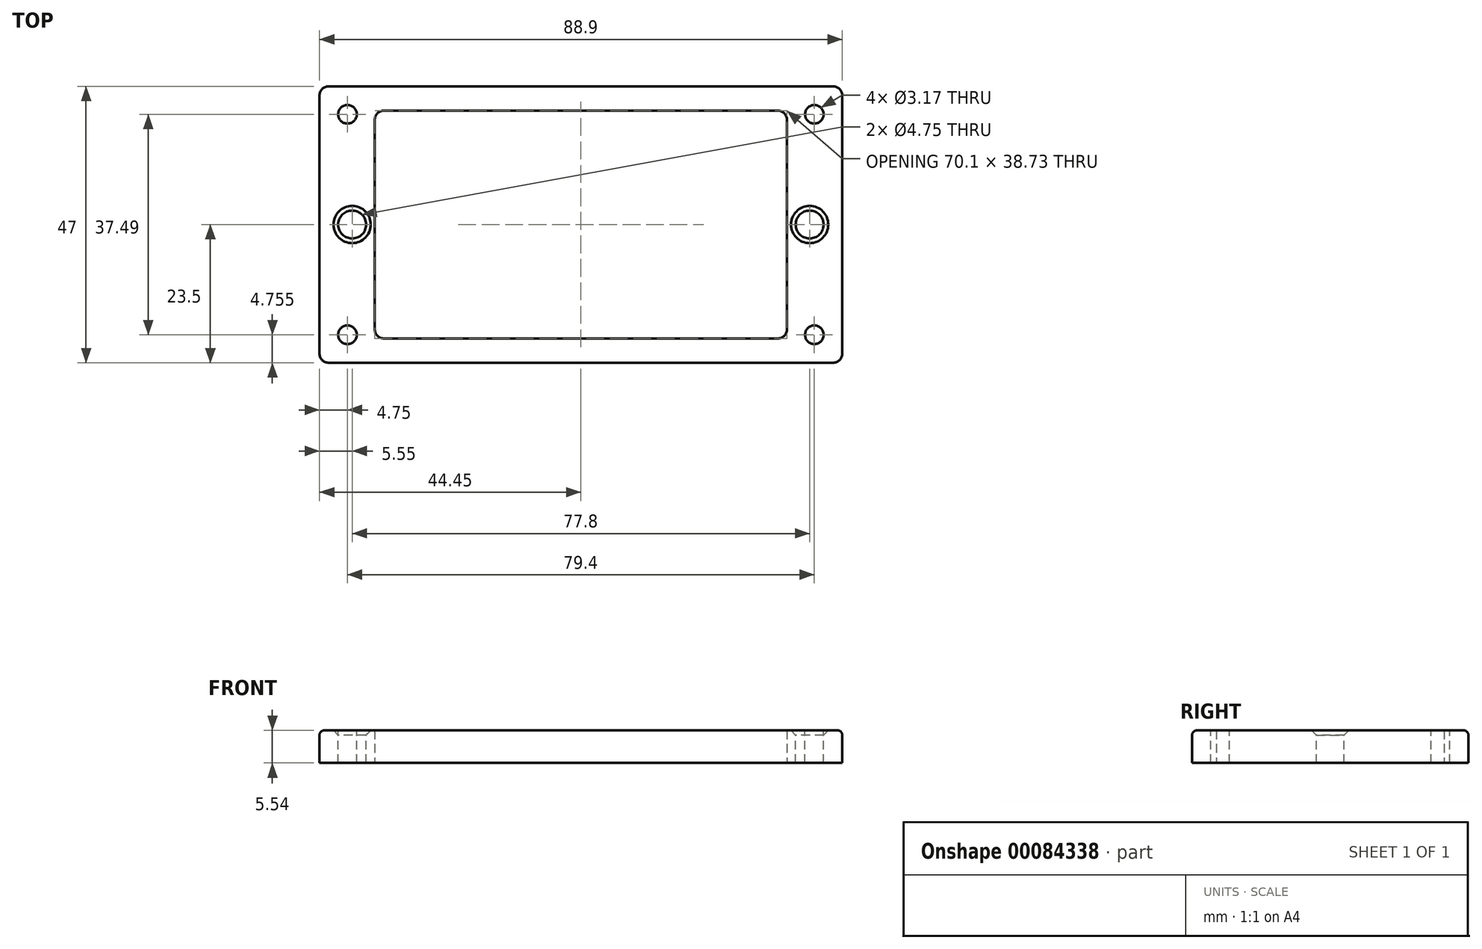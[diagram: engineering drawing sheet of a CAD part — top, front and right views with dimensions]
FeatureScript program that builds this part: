
annotation { "Feature Type Name" : "Feature", "Feature Type Description" : "" }
export const myFeature = defineFeature(function(context is Context, id is Id, definition is map)
    precondition{}
    {
        {
            var Q0;
            Q0=qCreatedBy(makeId("Top.planeOp"),FACE);
            var sketch = newSketch(context, id + "F0", { "sketchPlane" : qUnion([Q0]), "disableImprinting" : false});
            skLineSegment(sketch, "E0.bottom", {"start": v(44.45, 23.5) * mm, "end": v(-44.45, 23.5) * mm});
            skLineSegment(sketch, "E0.top", {"start": v(44.45, -23.5) * mm, "end": v(-44.45, -23.5) * mm});
            skLineSegment(sketch, "E0.left", {"start": v(44.45, 23.5) * mm, "end": v(44.45, -23.5) * mm});
            skLineSegment(sketch, "E0.right", {"start": v(-44.45, 23.5) * mm, "end": v(-44.45, -23.5) * mm});
            skPoint(sketch, "E0.middle", {"position": v(0, 0) * mm});
            skLineSegment(sketch, "E1.bottom", {"start": v(35.05, 19.37) * mm, "end": v(-35.05, 19.37) * mm});
            skLineSegment(sketch, "E1.top", {"start": v(35.05, -19.37) * mm, "end": v(-35.05, -19.37) * mm});
            skLineSegment(sketch, "E1.left", {"start": v(35.05, 19.37) * mm, "end": v(35.05, -19.37) * mm});
            skLineSegment(sketch, "E1.right", {"start": v(-35.05, 19.37) * mm, "end": v(-35.05, -19.37) * mm});
            skSolve(sketch);
        }
        {
            var Q0;
            Q0=makeQuery(id+"F0.imprint","IMPRINT",FACE,{"disambiguationData":[TD([[makeQuery(id+"F0.imprint","IMPRINT",EDGE,{"derivedFrom":sQuery(id+"F0.wireOp",EDGE,"E0.bottom")}),1.0]])]});
            var sketch = newSketch(context, id + "F1", { "sketchPlane" : qUnion([Q0]), "disableImprinting" : false});
            skLineSegment(sketch, "E2", {"start": v(-44.45, 0) * mm, "end": v(-35.05, 0) * mm, "construction": true});
            skLineSegment(sketch, "E3.0", {"start": v(-44.45, 23.5) * mm, "end": v(-44.45, -23.5) * mm});
            skLineSegment(sketch, "E4.0", {"start": v(-35.05, 19.37) * mm, "end": v(-35.05, -19.37) * mm});
            skPoint(sketch, "E5", {"position": v(-38.9, 0) * mm});
            skCircle(sketch, "E6", {"center": v(-38.9, 0) * mm, "radius": 2.37 * mm});
            skCircle(sketch, "E7.MirrorC", {"center": v(38.9, 0) * mm, "radius": 2.37 * mm});
            skSolve(sketch);
        }
        {
            var Q0;
            Q0=makeQuery(id+"F0.imprint","IMPRINT",FACE,{"disambiguationData":[TD([[makeQuery(id+"F0.imprint","IMPRINT",EDGE,{"derivedFrom":sQuery(id+"F0.wireOp",EDGE,"E0.bottom")}),1.0]])]});
            extrude(context, id + "F2", {"entities" : qUnion([Q0]), "depth" : 5.54 * mm, "symmetric" : true});
        }
        {
            var Q0;
            Q0 = qSketchRegion(id + "F1", true);
            extrude(context, id + "F3", {"entities" : qUnion([Q0]), "operationType" : NewBodyOperationType.REMOVE, "oppositeDirection" : true, "depth" : 25.4 * mm, "symmetric" : true});
        }
        {
            var Q0;
            Q0=makeQuery(id+"F2.opExtrude","CAP_FACE",FACE,{"disambiguationData":[OSD([sQuery(id+"F0.wireOp",EDGE,"E0.bottom"),sQuery(id+"F0.wireOp",EDGE,"E0.top"),sQuery(id+"F0.wireOp",EDGE,"E0.left"),sQuery(id+"F0.wireOp",EDGE,"E0.right"),sQuery(id+"F0.wireOp",EDGE,"E1.bottom"),sQuery(id+"F0.wireOp",EDGE,"E1.top"),sQuery(id+"F0.wireOp",EDGE,"E1.left"),sQuery(id+"F0.wireOp",EDGE,"E1.right")])],"isStart":false});
            var sketch = newSketch(context, id + "F4", { "sketchPlane" : qUnion([Q0])});
            skCircle(sketch, "E8", {"center": v(-39.7, 18.75) * mm, "radius": 1.59 * mm});
            skCircle(sketch, "E9.MirrorC", {"center": v(-39.7, -18.75) * mm, "radius": 1.59 * mm});
            skCircle(sketch, "E10.MirrorC", {"center": v(39.7, 18.75) * mm, "radius": 1.59 * mm});
            skCircle(sketch, "E11.MirrorC", {"center": v(39.7, -18.75) * mm, "radius": 1.59 * mm});
            skSolve(sketch);
        }
        {
            var Q0;
            Q0 = qSketchRegion(id + "F4", true);
            extrude(context, id + "F5", {"entities" : qUnion([Q0]), "operationType" : NewBodyOperationType.REMOVE, "oppositeDirection" : true, "depth" : 25.4 * mm});
        }
        {
            var Q0;
            Q0=makeQuery(id+"F2.opExtrude","SWEPT_EDGE",EDGE,{"disambiguationData":[OSD([sQuery(id+"F0.wireOp",EDGE,"E0.bottom"),sQuery(id+"F0.wireOp",EDGE,"E0.right")])]});
            var Q1;
            Q1=makeQuery(id+"F2.opExtrude","SWEPT_EDGE",EDGE,{"disambiguationData":[OSD([sQuery(id+"F0.wireOp",EDGE,"E0.top"),sQuery(id+"F0.wireOp",EDGE,"E0.right")])]});
            var Q2;
            Q2=makeQuery(id+"F2.opExtrude","SWEPT_EDGE",EDGE,{"disambiguationData":[OSD([sQuery(id+"F0.wireOp",EDGE,"E0.bottom"),sQuery(id+"F0.wireOp",EDGE,"E0.left")])]});
            var Q3;
            Q3=makeQuery(id+"F2.opExtrude","SWEPT_EDGE",EDGE,{"disambiguationData":[OSD([sQuery(id+"F0.wireOp",EDGE,"E0.top"),sQuery(id+"F0.wireOp",EDGE,"E0.left")])]});
            var Q4;
            Q4=makeQuery(id+"F2.opExtrude","SWEPT_EDGE",EDGE,{"disambiguationData":[OSD([sQuery(id+"F0.wireOp",EDGE,"E1.bottom"),sQuery(id+"F0.wireOp",EDGE,"E1.left")])]});
            var Q5;
            Q5=makeQuery(id+"F2.opExtrude","SWEPT_EDGE",EDGE,{"disambiguationData":[OSD([sQuery(id+"F0.wireOp",EDGE,"E1.top"),sQuery(id+"F0.wireOp",EDGE,"E1.left")])]});
            var Q6;
            Q6=makeQuery(id+"F2.opExtrude","SWEPT_EDGE",EDGE,{"disambiguationData":[OSD([sQuery(id+"F0.wireOp",EDGE,"E1.bottom"),sQuery(id+"F0.wireOp",EDGE,"E1.right")])]});
            var Q7;
            Q7=makeQuery(id+"F2.opExtrude","SWEPT_EDGE",EDGE,{"disambiguationData":[OSD([sQuery(id+"F0.wireOp",EDGE,"E1.top"),sQuery(id+"F0.wireOp",EDGE,"E1.right")])]});
            fillet(context, id + "F6", {"entities" : qUnion([Q0, Q1, Q2, Q3, Q4, Q5, Q6, Q7]), "radius" : 1.57 * mm, "tangentPropagation" : true, "allowEdgeOverflow" : false});
        }
        {
            var Q0;
            Q0=makeQuery(id+"F2.opExtrude","CAP_EDGE",EDGE,{"disambiguationData":[OSD([sQuery(id+"F0.wireOp",EDGE,"E0.bottom")])],"isStart":false});
            var Q1;
            {var subQ0=sQuery(id+"F0.wireOp",EDGE,"E0.right");var subQ1=sQuery(id+"F0.wireOp",EDGE,"E0.bottom");Q1=makeQuery(id+"F6.opFillet","BLEND_EDGE",EDGE,{"blendedFrom":[makeQuery(id+"F2.opExtrude","SWEPT_EDGE",EDGE,{"disambiguationData":[OSD([subQ1,subQ0])]}),makeQuery(id+"F2.opExtrude","CAP_FACE",FACE,{"disambiguationData":[OSD([subQ1,sQuery(id+"F0.wireOp",EDGE,"E0.top"),sQuery(id+"F0.wireOp",EDGE,"E0.left"),subQ0,sQuery(id+"F0.wireOp",EDGE,"E1.bottom"),sQuery(id+"F0.wireOp",EDGE,"E1.top"),sQuery(id+"F0.wireOp",EDGE,"E1.left"),sQuery(id+"F0.wireOp",EDGE,"E1.right")])],"isStart":false})],"blendedInto":[makeQuery(id+"F2.opExtrude","CAP_FACE",FACE,{"disambiguationData":[OSD([subQ1,sQuery(id+"F0.wireOp",EDGE,"E0.top"),sQuery(id+"F0.wireOp",EDGE,"E0.left"),subQ0,sQuery(id+"F0.wireOp",EDGE,"E1.bottom"),sQuery(id+"F0.wireOp",EDGE,"E1.top"),sQuery(id+"F0.wireOp",EDGE,"E1.left"),sQuery(id+"F0.wireOp",EDGE,"E1.right")])],"isStart":false})]});}
            var Q2;
            Q2=makeQuery(id+"F2.opExtrude","CAP_EDGE",EDGE,{"disambiguationData":[OSD([sQuery(id+"F0.wireOp",EDGE,"E0.right")])],"isStart":false});
            var Q3;
            {var subQ0=sQuery(id+"F0.wireOp",EDGE,"E0.right");var subQ1=sQuery(id+"F0.wireOp",EDGE,"E0.top");Q3=makeQuery(id+"F6.opFillet","BLEND_EDGE",EDGE,{"blendedFrom":[makeQuery(id+"F2.opExtrude","SWEPT_EDGE",EDGE,{"disambiguationData":[OSD([subQ1,subQ0])]}),makeQuery(id+"F2.opExtrude","CAP_FACE",FACE,{"disambiguationData":[OSD([sQuery(id+"F0.wireOp",EDGE,"E0.bottom"),subQ1,sQuery(id+"F0.wireOp",EDGE,"E0.left"),subQ0,sQuery(id+"F0.wireOp",EDGE,"E1.bottom"),sQuery(id+"F0.wireOp",EDGE,"E1.top"),sQuery(id+"F0.wireOp",EDGE,"E1.left"),sQuery(id+"F0.wireOp",EDGE,"E1.right")])],"isStart":false})],"blendedInto":[makeQuery(id+"F2.opExtrude","CAP_FACE",FACE,{"disambiguationData":[OSD([sQuery(id+"F0.wireOp",EDGE,"E0.bottom"),subQ1,sQuery(id+"F0.wireOp",EDGE,"E0.left"),subQ0,sQuery(id+"F0.wireOp",EDGE,"E1.bottom"),sQuery(id+"F0.wireOp",EDGE,"E1.top"),sQuery(id+"F0.wireOp",EDGE,"E1.left"),sQuery(id+"F0.wireOp",EDGE,"E1.right")])],"isStart":false})]});}
            var Q4;
            Q4=makeQuery(id+"F2.opExtrude","CAP_EDGE",EDGE,{"disambiguationData":[OSD([sQuery(id+"F0.wireOp",EDGE,"E0.top")])],"isStart":false});
            var Q5;
            {var subQ0=sQuery(id+"F0.wireOp",EDGE,"E0.left");var subQ1=sQuery(id+"F0.wireOp",EDGE,"E0.top");Q5=makeQuery(id+"F6.opFillet","BLEND_EDGE",EDGE,{"blendedFrom":[makeQuery(id+"F2.opExtrude","SWEPT_EDGE",EDGE,{"disambiguationData":[OSD([subQ1,subQ0])]}),makeQuery(id+"F2.opExtrude","CAP_FACE",FACE,{"disambiguationData":[OSD([sQuery(id+"F0.wireOp",EDGE,"E0.bottom"),subQ1,subQ0,sQuery(id+"F0.wireOp",EDGE,"E0.right"),sQuery(id+"F0.wireOp",EDGE,"E1.bottom"),sQuery(id+"F0.wireOp",EDGE,"E1.top"),sQuery(id+"F0.wireOp",EDGE,"E1.left"),sQuery(id+"F0.wireOp",EDGE,"E1.right")])],"isStart":false})],"blendedInto":[makeQuery(id+"F2.opExtrude","CAP_FACE",FACE,{"disambiguationData":[OSD([sQuery(id+"F0.wireOp",EDGE,"E0.bottom"),subQ1,subQ0,sQuery(id+"F0.wireOp",EDGE,"E0.right"),sQuery(id+"F0.wireOp",EDGE,"E1.bottom"),sQuery(id+"F0.wireOp",EDGE,"E1.top"),sQuery(id+"F0.wireOp",EDGE,"E1.left"),sQuery(id+"F0.wireOp",EDGE,"E1.right")])],"isStart":false})]});}
            var Q6;
            Q6=makeQuery(id+"F2.opExtrude","CAP_EDGE",EDGE,{"disambiguationData":[OSD([sQuery(id+"F0.wireOp",EDGE,"E0.left")])],"isStart":false});
            var Q7;
            {var subQ0=sQuery(id+"F0.wireOp",EDGE,"E0.left");var subQ1=sQuery(id+"F0.wireOp",EDGE,"E0.bottom");Q7=makeQuery(id+"F6.opFillet","BLEND_EDGE",EDGE,{"blendedFrom":[makeQuery(id+"F2.opExtrude","SWEPT_EDGE",EDGE,{"disambiguationData":[OSD([subQ1,subQ0])]}),makeQuery(id+"F2.opExtrude","CAP_FACE",FACE,{"disambiguationData":[OSD([subQ1,sQuery(id+"F0.wireOp",EDGE,"E0.top"),subQ0,sQuery(id+"F0.wireOp",EDGE,"E0.right"),sQuery(id+"F0.wireOp",EDGE,"E1.bottom"),sQuery(id+"F0.wireOp",EDGE,"E1.top"),sQuery(id+"F0.wireOp",EDGE,"E1.left"),sQuery(id+"F0.wireOp",EDGE,"E1.right")])],"isStart":false})],"blendedInto":[makeQuery(id+"F2.opExtrude","CAP_FACE",FACE,{"disambiguationData":[OSD([subQ1,sQuery(id+"F0.wireOp",EDGE,"E0.top"),subQ0,sQuery(id+"F0.wireOp",EDGE,"E0.right"),sQuery(id+"F0.wireOp",EDGE,"E1.bottom"),sQuery(id+"F0.wireOp",EDGE,"E1.top"),sQuery(id+"F0.wireOp",EDGE,"E1.left"),sQuery(id+"F0.wireOp",EDGE,"E1.right")])],"isStart":false})]});}
            fillet(context, id + "F7", {"entities" : qUnion([Q0, Q1, Q2, Q3, Q4, Q5, Q6, Q7]), "radius" : 0.79 * mm, "tangentPropagation" : true, "allowEdgeOverflow" : false});
        }
        {
            var Q0;
            Q0=makeQuery(id+"F5.boolean.opBoolean","COPY",EDGE,{"derivedFrom":makeQuery(id+"F5.opExtrude","CAP_EDGE",EDGE,{"disambiguationData":[OSD([sQuery(id+"F4.wireOp",EDGE,"E8")])],"isStart":true})});
            var Q1;
            Q1=makeQuery(id+"F3.boolean.opBoolean","INTERSECT",EDGE,{"derivedFrom":[makeQuery(id+"F2.opExtrude","CAP_FACE",FACE,{"disambiguationData":[OSD([sQuery(id+"F0.wireOp",EDGE,"E0.bottom"),sQuery(id+"F0.wireOp",EDGE,"E0.top"),sQuery(id+"F0.wireOp",EDGE,"E0.left"),sQuery(id+"F0.wireOp",EDGE,"E0.right"),sQuery(id+"F0.wireOp",EDGE,"E1.bottom"),sQuery(id+"F0.wireOp",EDGE,"E1.top"),sQuery(id+"F0.wireOp",EDGE,"E1.left"),sQuery(id+"F0.wireOp",EDGE,"E1.right")])],"isStart":false}),makeQuery(id+"F3.opExtrude","SWEPT_FACE",FACE,{"disambiguationData":[OSD([sQuery(id+"F1.wireOp",EDGE,"E6")])]})]});
            var Q2;
            Q2=makeQuery(id+"F5.boolean.opBoolean","COPY",EDGE,{"derivedFrom":makeQuery(id+"F5.opExtrude","CAP_EDGE",EDGE,{"disambiguationData":[OSD([sQuery(id+"F4.wireOp",EDGE,"E9.MirrorC")])],"isStart":true})});
            var Q3;
            Q3=makeQuery(id+"F5.boolean.opBoolean","COPY",EDGE,{"derivedFrom":makeQuery(id+"F5.opExtrude","CAP_EDGE",EDGE,{"disambiguationData":[OSD([sQuery(id+"F4.wireOp",EDGE,"E10.MirrorC")])],"isStart":true})});
            var Q4;
            Q4=makeQuery(id+"F3.boolean.opBoolean","INTERSECT",EDGE,{"derivedFrom":[makeQuery(id+"F2.opExtrude","CAP_FACE",FACE,{"disambiguationData":[OSD([sQuery(id+"F0.wireOp",EDGE,"E0.bottom"),sQuery(id+"F0.wireOp",EDGE,"E0.top"),sQuery(id+"F0.wireOp",EDGE,"E0.left"),sQuery(id+"F0.wireOp",EDGE,"E0.right"),sQuery(id+"F0.wireOp",EDGE,"E1.bottom"),sQuery(id+"F0.wireOp",EDGE,"E1.top"),sQuery(id+"F0.wireOp",EDGE,"E1.left"),sQuery(id+"F0.wireOp",EDGE,"E1.right")])],"isStart":false}),makeQuery(id+"F3.opExtrude","SWEPT_FACE",FACE,{"disambiguationData":[OSD([sQuery(id+"F1.wireOp",EDGE,"E7.MirrorC")])]})]});
            var Q5;
            Q5=makeQuery(id+"F5.boolean.opBoolean","COPY",EDGE,{"derivedFrom":makeQuery(id+"F5.opExtrude","CAP_EDGE",EDGE,{"disambiguationData":[OSD([sQuery(id+"F4.wireOp",EDGE,"E11.MirrorC")])],"isStart":true})});
            chamfer(context, id + "F8", {"entities" : qUnion([Q0, Q1, Q2, Q3, Q4, Q5]), "width" : 0.79 * mm, "tangentPropagation" : true});
        }
    });
